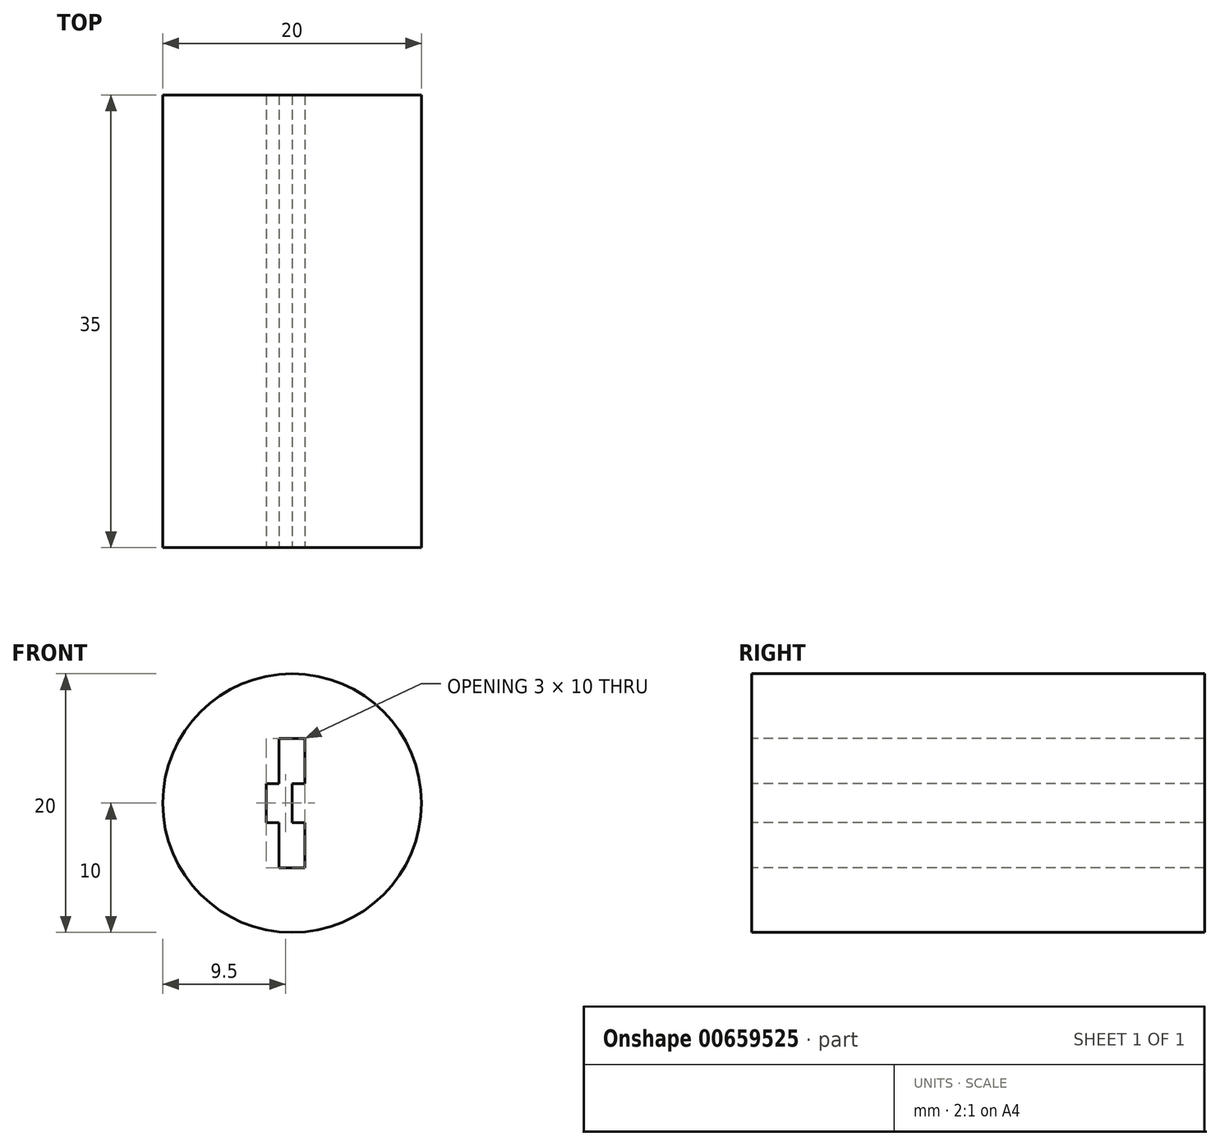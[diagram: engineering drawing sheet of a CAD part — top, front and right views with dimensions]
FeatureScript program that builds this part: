
annotation { "Feature Type Name" : "Feature", "Feature Type Description" : "" }
export const myFeature = defineFeature(function(context is Context, id is Id, definition is map)
    precondition{}
    {
        {
            var Q0;
            Q0=qCreatedBy(makeId("Front.planeOp"),FACE);
            var sketch = newSketch(context, id + "F0", { "sketchPlane" : qUnion([Q0])});
            skCircle(sketch, "E0", {"center": v(0, 0) * mm, "radius": 10 * mm});
            skSolve(sketch);
        }
        {
            var Q0;
            Q0=makeQuery(id+"F0.imprint","IMPRINT",FACE,{"disambiguationData":[TD([[makeQuery(id+"F0.imprint","IMPRINT",EDGE,{"derivedFrom":sQuery(id+"F0.wireOp",EDGE,"E0")}),1.0]])]});
            extrude(context, id + "F1", {"entities" : qUnion([Q0]), "depth" : 35 * mm, "offsetDistance" : 25 * mm});
        }
        {
            var Q0;
            Q0=qCreatedBy(makeId("Top.planeOp"),FACE);
            var sketch = newSketch(context, id + "F2", { "sketchPlane" : qUnion([Q0])});
            skCircle(sketch, "E1", {"center": v(0, -5.5) * mm, "radius": 2.5 * mm});
            skCircle(sketch, "E2", {"center": v(0, -13.5) * mm, "radius": 2.5 * mm});
            skCircle(sketch, "E3", {"center": v(0, -21.5) * mm, "radius": 2.5 * mm});
            skCircle(sketch, "E4", {"center": v(0, -29.5) * mm, "radius": 2.5 * mm});
            skSolve(sketch);
        }
        {
            var Q0;
            Q0=makeQuery(id+"F1.opExtrude","CAP_FACE",FACE,{"disambiguationData":[OSD([sQuery(id+"F0.wireOp",EDGE,"E0")])],"isStart":false});
            var sketch = newSketch(context, id + "F3", { "sketchPlane" : qUnion([Q0])});
            skLineSegment(sketch, "E5", {"start": v(1, 5) * mm, "end": v(1, 1.5) * mm});
            skLineSegment(sketch, "E6", {"start": v(1, 1.5) * mm, "end": v(0, 1.5) * mm});
            skLineSegment(sketch, "E7", {"start": v(0, 1.5) * mm, "end": v(0, -1.5) * mm});
            skLineSegment(sketch, "E8", {"start": v(0, -1.5) * mm, "end": v(1, -1.5) * mm});
            skLineSegment(sketch, "E9", {"start": v(1, -1.5) * mm, "end": v(1, -5) * mm});
            skLineSegment(sketch, "E10", {"start": v(-1, 5) * mm, "end": v(-1, 1.5) * mm});
            skLineSegment(sketch, "E11", {"start": v(-1, 1.5) * mm, "end": v(-2, 1.5) * mm});
            skLineSegment(sketch, "E12", {"start": v(-2, 1.5) * mm, "end": v(-2, -1.5) * mm});
            skLineSegment(sketch, "E13", {"start": v(-2, -1.5) * mm, "end": v(-1, -1.5) * mm});
            skLineSegment(sketch, "E14", {"start": v(-1, -1.5) * mm, "end": v(-1, -5) * mm});
            skLineSegment(sketch, "E15", {"start": v(-1, 5) * mm, "end": v(1, 5) * mm});
            skLineSegment(sketch, "E16", {"start": v(-1, -5) * mm, "end": v(1, -5) * mm});
            skSolve(sketch);
        }
        {
            var Q0;
            Q0 = qSketchRegion(id + "F3", true);
            var Q1;
            Q1=makeQuery(id+"F1.opExtrude","CAP_FACE",FACE,{"disambiguationData":[OSD([sQuery(id+"F0.wireOp",EDGE,"E0")])],"isStart":true});
            extrude(context, id + "F4", {"entities" : qUnion([Q0]), "operationType" : NewBodyOperationType.REMOVE, "endBound" : BoundingType.UP_TO_SURFACE, "oppositeDirection" : true, "depth" : 25 * mm, "endBoundEntityFace" : qUnion([Q1]), "offsetDistance" : 25 * mm});
        }
    });
